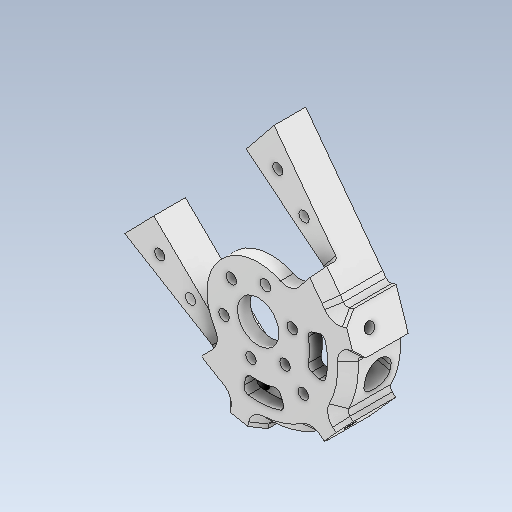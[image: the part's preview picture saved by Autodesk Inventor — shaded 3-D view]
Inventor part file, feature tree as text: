
AUTODESK INVENTOR PART (.ipt)
format: ipt  version: 2020 (Build 240168000, 168)  size: 716,800 bytes
history: native  units: mm
features: sketch x19, extrude x19, projected_geometry x16, plane x8, fillet x5, reference x5, other x5, chamfer x1, mirror x1
ambient origin geometry x8: Origin, YZ Plane, XZ Plane, XY Plane, X Axis, Y Axis, Z Axis, Center Point
bodies: Solid1 (feature_tree)
feature tree (79):
  plane  "Work Plane1"
  sketch  "Sketch1"  dims[d0=70.0mm d1=58.0mm]
  plane  "Work Plane2"
  extrude  "Extrusion1"  Depth=58.0mm
  sketch  "Sketch2"  dims[d2=10.0mm d3=0.0mm d4=40.0mm]
  plane  "Work Plane3"
  extrude  "Extrusion2"  Depth=10.0mm
  sketch  "Sketch3"  dims[d5=40.0mm d6=10.0mm d7=0.0mm]
  plane  "Work Plane4"
  extrude  "Extrusion3"  Depth=10.0mm TaperAngle=0.0deg
  extrude  "Extrusion4"  Depth=10.0mm TaperAngle=0.0deg
  plane  "Work Plane5"
  extrude  "Extrusion5"  Depth=5.0mm TaperAngle=0.0deg
  extrude  "Extrusion7"  Depth=40.0mm
  extrude  "Extrusion8"  Depth=5.0mm
  extrude  "Extrusion9"  Depth=5.0mm TaperAngle=360.0deg
  extrude  "Extrusion10"  Depth=4.0mm
  fillet  "Fillet1"  Radius=4.1mm
  extrude  "Extrusion11"  Depth=5.0mm TaperAngle=0.0deg
  extrude  "Extrusion12"  Depth=5.0mm TaperAngle=0.0deg
  fillet  "Fillet3"  Radius=58.0mm
  chamfer  "Chamfer2"  Distance=5.0mm
  extrude  "Extrusion13"  Depth=4.0mm TaperAngle=45.0deg
  extrude  "Extrusion14"  Depth=4.0mm TaperAngle=0.0deg
  extrude  "Extrusion15"  Depth=4.0mm TaperAngle=0.0deg
  fillet  "Fillet4"  Radius=4.0mm
  fillet  "Fillet5"  Radius=12.0mm
  plane  "Work Plane6"
  extrude  "Extrusion16"  Depth=6.0mm
  plane  "Work Plane7"
  extrude  "Extrusion17"  Depth=10.0mm
  extrude  "Extrusion18"  Depth=1.0mm
  extrude  "Extrusion19"  Depth=10.0mm TaperAngle=0.0deg
  fillet  "Fillet6"  Radius=14.0mm
  plane  "Work Plane8"
  mirror  "Mirror1"
  extrude  "Extrusion20"  Depth=10.0mm TaperAngle=360.0deg
  reference  "Reference1"
  reference  "Reference2"
  reference  "Reference3"
  projected_geometry  "Projected Loop1"
  projected_geometry  "Projected Loop2"
  sketch  "Sketch4"  dims[d8=10.0mm d9=0.0mm d10=10.0mm d11=0.0mm]
  reference  "Reference4"
  projected_geometry  "Projected Loop3"
  sketch  "Sketch5"  dims[d12=5.0mm d13=0.0mm d24=14.0mm d25=0.0mm]
  projected_geometry  "Projected Loop4"
  sketch  "Sketch8"  dims[d26=16.15mm d27=40.0mm]
  reference  "Reference5"
  sketch  "Sketch9"  dims[d28=5.0mm d29=0.0mm d30=15.0mm]
  projected_geometry  "Projected Loop7"
  sketch  "Sketch10"  dims[d31=5.0mm d32=60.0mm d34=360.0deg]
  projected_geometry  "Projected Loop8"
  sketch  "Sketch11"  dims[d36=10.0mm d37=0.0mm d38=4.0mm d39=4.1mm]
  projected_geometry  "Projected Loop9"
  sketch  "Sketch12"  dims[d40=60.0mm d42=360.0deg d44=5.0mm d45=0.0mm]
  projected_geometry  "Projected Loop10"
  projected_geometry  "Projected Loop11"
  sketch  "Sketch13"  dims[d46=2.0mm d51=5.0mm d52=0.0mm d53=58.0mm d54=5.0mm d55=0.0mm]
  projected_geometry  "Projected Loop12"
  projected_geometry  "Projected Loop13"
  sketch  "Sketch14"  dims[d56=2.0mm d57=4.0mm d58=2.0mm d59=45.0deg]
  sketch  "Sketch15"  dims[d60=4.0mm d61=12.0mm d62=0.0mm]
  sketch  "Sketch16"  dims[d63=4.0mm d64=12.0mm d65=0.0mm d66=4.0mm d67=12.0mm d68=0.0mm]
  projected_geometry  "Projected Loop14"
  sketch  "Sketch17"  dims[d69=1.2mm d70=6.0mm]
  projected_geometry  "Projected Loop15"
  sketch  "Sketch18"  dims[d71=1.0mm d72=10.0mm]
  projected_geometry  "Projected Loop16"
  sketch  "Sketch19"  dims[d73=12.0mm d74=0.0mm d75=1.0mm]
  projected_geometry  "Projected Loop17"
  sketch  "Sketch20"  dims[d76=10.0mm d77=12.0mm d78=0.0mm d79=14.0mm]
  projected_geometry  "Projected Loop18"
  sketch  "Sketch21"  dims[d80=4.1mm d81=60.0mm d83=360.0deg d85=10.0mm d86=0.0mm d87=40.0mm d88=4.18879mm d89=10.0mm d90=0.0mm d91=2.0mm d92=9.5mm d93=4.1mm d94=10.0mm d95=0.0mm d33=0.872665mm d35=0.872665mm d96=0.5mm d97=0.872665mm]
  parser-record x1  (decoder bookkeeping rows leaked as tree rows — omitted from the tree; the rows remain in map.json)
  other  "reducer_3.iam"
  other  "motor_h_4:1"
  other  "xl_30_1:1"
  other  "motor_r_1:1"
note: 1 file-system path scrubbed to <path> (originals preserved in map.json)
